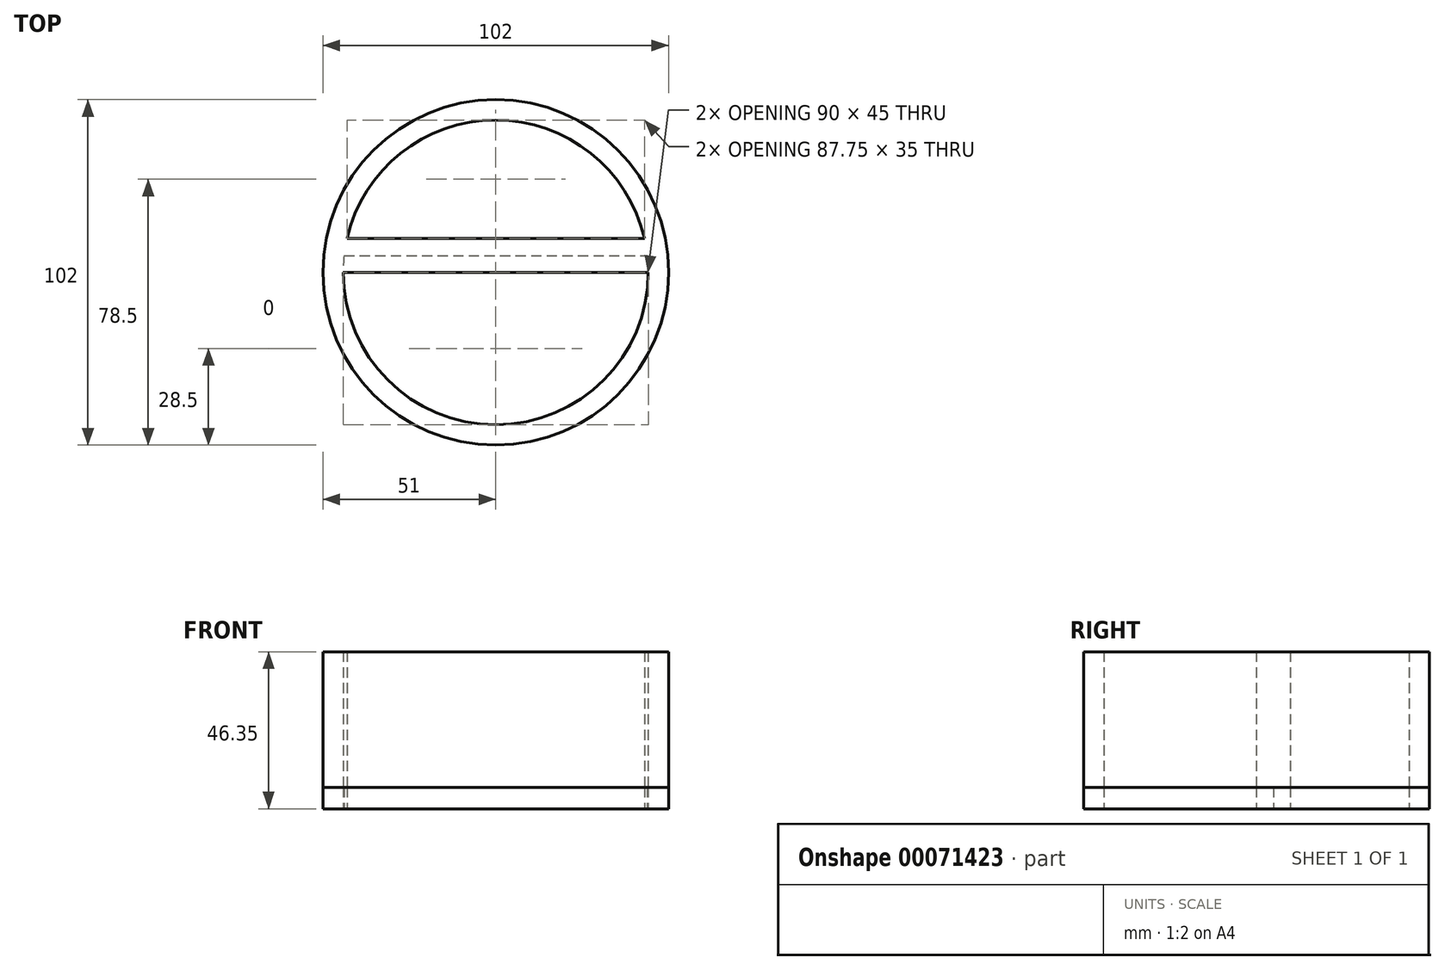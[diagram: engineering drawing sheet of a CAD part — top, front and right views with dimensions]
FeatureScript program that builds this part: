
annotation { "Feature Type Name" : "Feature", "Feature Type Description" : "" }
export const myFeature = defineFeature(function(context is Context, id is Id, definition is map)
    precondition{}
    {
        {
            var Q0;
            Q0=qCreatedBy(makeId("Top.planeOp"),FACE);
            var sketch = newSketch(context, id + "F0", { "sketchPlane" : qUnion([Q0])});
            skCircle(sketch, "E0", {"center": v(0, 0) * mm, "radius": 51 * mm});
            skCircle(sketch, "E1", {"center": v(0, 0) * mm, "radius": 45 * mm});
            skLineSegment(sketch, "E2", {"start": v(-45, 0) * mm, "end": v(45, 0) * mm});
            skLineSegment(sketch, "E3", {"start": v(-51, 0) * mm, "end": v(51, 0) * mm});
            skLineSegment(sketch, "E4", {"start": v(-50.75, 5) * mm, "end": v(50.75, 5) * mm});
            skLineSegment(sketch, "E5", {"start": v(-50, 10) * mm, "end": v(50, 10) * mm});
            skSolve(sketch);
        }
        {
            var Q0;
            {var subQ0=sQuery(id+"F0.wireOp",EDGE,"E2");Q0=makeQuery(id+"F0.imprint","IMPRINT",FACE,{"disambiguationData":[TD([[makeQuery(id+"F0.imprint","IMPRINT",EDGE,{"derivedFrom":subQ0}),1.0]])]});}
            var Q1;
            Q1=makeQuery(id+"F0.imprint","IMPRINT",FACE,{"disambiguationData":[TD([[makeQuery(id+"F0.imprint","IMPRINT",EDGE,{"derivedFrom":sQuery(id+"F0.wireOp",EDGE,"E0")}),1.0]])]});
            var Q2;
            {var subQ0=sQuery(id+"F0.wireOp",EDGE,"E4");var subQ1=sQuery(id+"F0.wireOp",EDGE,"E1");var subQ2=makeQuery(id+"F0.imprint","INTERSECT",VERTEX,{"disambiguationData":[OD(0.0)],"derivedFrom":[subQ1,subQ0]});Q2=makeQuery(id+"F0.imprint","IMPRINT",FACE,{"disambiguationData":[TD([[makeQuery(id+"F0.imprint","IMPRINT",EDGE,{"disambiguationData":[TD([[subQ2,-1.0]])],"derivedFrom":subQ1}),1.0]])]});}
            var Q3;
            {var subQ0=sQuery(id+"F0.wireOp",EDGE,"E4");var subQ1=sQuery(id+"F0.wireOp",EDGE,"E1");var subQ2=makeQuery(id+"F0.imprint","INTERSECT",VERTEX,{"disambiguationData":[OD(0.0)],"derivedFrom":[subQ1,subQ0]});Q3=makeQuery(id+"F0.imprint","IMPRINT",FACE,{"disambiguationData":[TD([[makeQuery(id+"F0.imprint","IMPRINT",EDGE,{"disambiguationData":[TD([[subQ2,1.0]])],"derivedFrom":subQ1}),1.0]])]});}
            var Q4;
            {var subQ0=sQuery(id+"F0.wireOp",EDGE,"E5");var subQ1=sQuery(id+"F0.wireOp",EDGE,"E1");var subQ2=makeQuery(id+"F0.imprint","INTERSECT",VERTEX,{"disambiguationData":[OD(0.0)],"derivedFrom":[subQ1,subQ0]});Q4=makeQuery(id+"F0.imprint","IMPRINT",FACE,{"disambiguationData":[TD([[makeQuery(id+"F0.imprint","IMPRINT",EDGE,{"disambiguationData":[TD([[subQ2,-1.0]])],"derivedFrom":subQ1}),1.0]])]});}
            extrude(context, id + "F1", {"entities" : qUnion([Q0, Q1, Q2, Q3, Q4]), "depth" : 6.35 * mm});
        }
        {
            var Q0;
            {var subQ0=sQuery(id+"F0.wireOp",EDGE,"E3");var subQ1=sQuery(id+"F0.wireOp",EDGE,"E1");var subQ2=makeQuery(id+"F0.imprint","INTERSECT",VERTEX,{"disambiguationData":[OD(0.0)],"derivedFrom":[subQ1,subQ0]});Q0=makeQuery(id+"F0.imprint","IMPRINT",FACE,{"disambiguationData":[TD([[makeQuery(id+"F0.imprint","IMPRINT",EDGE,{"disambiguationData":[TD([[subQ2,1.0]])],"derivedFrom":subQ1}),1.0]])]});}
            extrude(context, id + "F2", {"entities" : qUnion([Q0]), "depth" : 6.35 * mm});
        }
        {
            var Q0;
            {var subQ0=sQuery(id+"F0.wireOp",EDGE,"E5");var subQ1=sQuery(id+"F0.wireOp",EDGE,"E0");var subQ2=makeQuery(id+"F0.imprint","INTERSECT",VERTEX,{"disambiguationData":[OD(0.0)],"derivedFrom":[subQ1,subQ0]});Q0=makeQuery(id+"F0.imprint","IMPRINT",FACE,{"disambiguationData":[TD([[makeQuery(id+"F0.imprint","IMPRINT",EDGE,{"disambiguationData":[TD([[subQ2,1.0]])],"derivedFrom":subQ1}),1.0]])]});}
            var Q1;
            {var subQ0=sQuery(id+"F0.wireOp",EDGE,"E4");var subQ1=sQuery(id+"F0.wireOp",EDGE,"E0");var subQ2=makeQuery(id+"F0.imprint","INTERSECT",VERTEX,{"disambiguationData":[OD(0.0)],"derivedFrom":[subQ1,subQ0]});Q1=makeQuery(id+"F0.imprint","IMPRINT",FACE,{"disambiguationData":[TD([[makeQuery(id+"F0.imprint","IMPRINT",EDGE,{"disambiguationData":[TD([[subQ2,1.0]])],"derivedFrom":subQ1}),1.0]])]});}
            var Q2;
            {var subQ0=sQuery(id+"F0.wireOp",EDGE,"E4");var subQ1=sQuery(id+"F0.wireOp",EDGE,"E1");var subQ2=makeQuery(id+"F0.imprint","INTERSECT",VERTEX,{"disambiguationData":[OD(0.0)],"derivedFrom":[subQ1,subQ0]});Q2=makeQuery(id+"F0.imprint","IMPRINT",FACE,{"disambiguationData":[TD([[makeQuery(id+"F0.imprint","IMPRINT",EDGE,{"disambiguationData":[TD([[subQ2,-1.0]])],"derivedFrom":subQ1}),1.0]])]});}
            var Q3;
            {var subQ0=sQuery(id+"F0.wireOp",EDGE,"E4");var subQ1=sQuery(id+"F0.wireOp",EDGE,"E0");var subQ2=makeQuery(id+"F0.imprint","INTERSECT",VERTEX,{"disambiguationData":[OD(1.0)],"derivedFrom":[subQ1,subQ0]});Q3=makeQuery(id+"F0.imprint","IMPRINT",FACE,{"disambiguationData":[TD([[makeQuery(id+"F0.imprint","IMPRINT",EDGE,{"disambiguationData":[TD([[subQ2,-1.0]])],"derivedFrom":subQ1}),1.0]])]});}
            var Q4;
            Q4=makeQuery(id+"F1.opExtrude","CAP_FACE",FACE,{"disambiguationData":[OSD([sQuery(id+"F0.wireOp",EDGE,"E0"),sQuery(id+"F0.wireOp",EDGE,"E1"),sQuery(id+"F0.wireOp",EDGE,"E3")])],"isStart":false});
            extrude(context, id + "F3", {"entities" : qUnion([Q0, Q1, Q2, Q3, Q4]), "depth" : 40 * mm});
        }
        {
            var Q0;
            Q0=makeQuery(id+"F3.opExtrude","SWEPT_BODY",BODY,{"disambiguationData":[OSD([sQuery(id+"F0.wireOp",EDGE,"E0"),sQuery(id+"F0.wireOp",EDGE,"E1"),sQuery(id+"F0.wireOp",EDGE,"E3")])]});
            deleteBodies(context, id + "F4", {"entities" : qUnion([Q0])});
        }
    });
